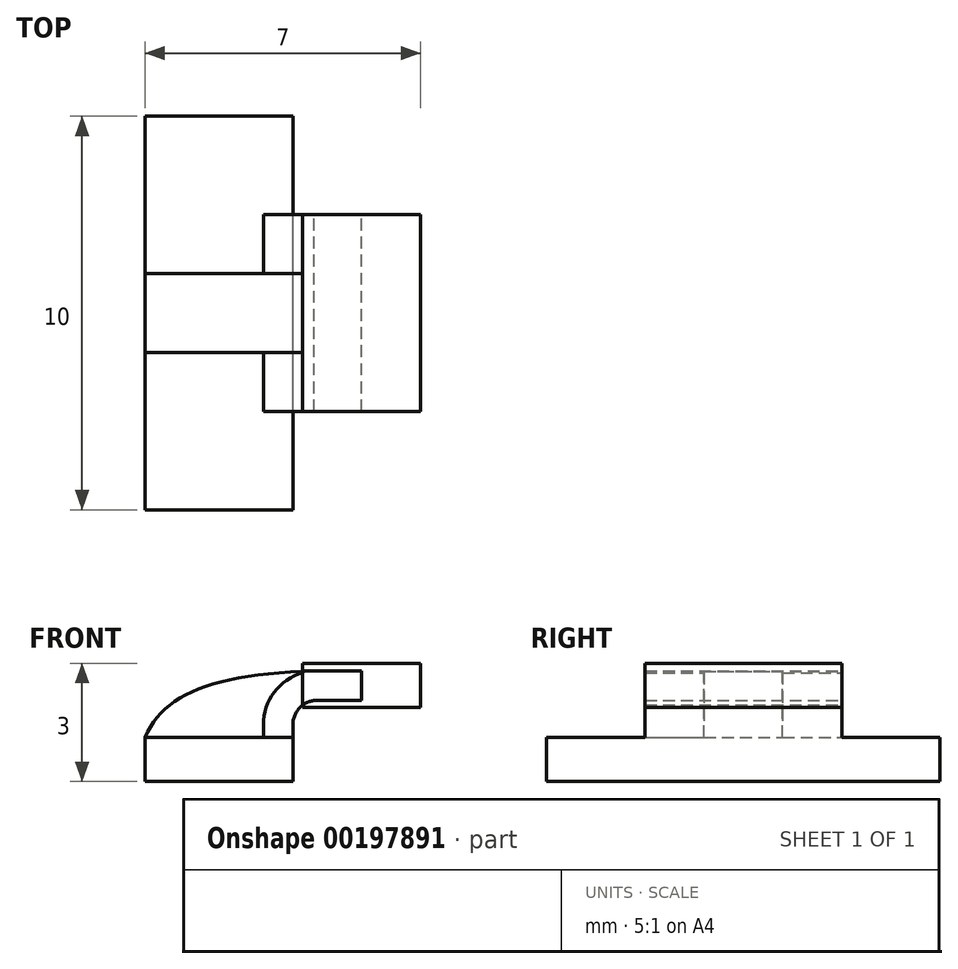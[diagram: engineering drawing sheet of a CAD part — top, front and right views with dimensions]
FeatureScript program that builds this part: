
annotation { "Feature Type Name" : "Feature", "Feature Type Description" : "" }
export const myFeature = defineFeature(function(context is Context, id is Id, definition is map)
    precondition{}
    {
        {
            var Q0;
            Q0=qCreatedBy(makeId("Front.planeOp"),FACE);
            var sketch = newSketch(context, id + "F0", { "sketchPlane" : qUnion([Q0])});
            skLineSegment(sketch, "E0.bottom", {"start": v(-1.87, -0.56) * mm, "end": v(1.88, -0.56) * mm});
            skLineSegment(sketch, "E0.top", {"start": v(-1.88, 0.56) * mm, "end": v(1.87, 0.56) * mm});
            skLineSegment(sketch, "E0.left", {"start": v(-1.87, -0.56) * mm, "end": v(-1.88, 0.56) * mm});
            skLineSegment(sketch, "E0.right", {"start": v(1.88, -0.56) * mm, "end": v(1.87, 0.56) * mm});
            skPoint(sketch, "E0.middle", {"position": v(0, 0) * mm});
            skLineSegment(sketch, "E1.bottom", {"start": v(2.12, 1.31) * mm, "end": v(5.12, 1.31) * mm});
            skLineSegment(sketch, "E1.top", {"start": v(2.12, 2.44) * mm, "end": v(5.12, 2.44) * mm});
            skLineSegment(sketch, "E1.left", {"start": v(2.12, 1.31) * mm, "end": v(2.12, 2.44) * mm});
            skLineSegment(sketch, "E1.right", {"start": v(5.12, 1.31) * mm, "end": v(5.12, 2.44) * mm});
            skPoint(sketch, "E1.middle", {"position": v(3.62, 1.87) * mm});
            skLineSegment(sketch, "E2", {"start": v(1.87, 0.56) * mm, "end": v(1.87, 0.88) * mm});
            skArc(sketch, "E3", {"start": v(1.87, 0.88) * mm, "mid": v(2.06, 1.32) * mm, "end": v(2.5, 1.5) * mm});
            skLineSegment(sketch, "E4", {"start": v(2.5, 1.5) * mm, "end": v(3.62, 1.5) * mm});
            skPoint(sketch, "E4.endSnap0", {"position": v(3.62, 1.31) * mm});
            skLineSegment(sketch, "E5.0", {"start": v(2.5, -3.5) * mm, "end": v(3.62, -3.5) * mm});
            skLineSegment(sketch, "E6.0", {"start": v(2.5, 2.25) * mm, "end": v(3.62, 2.25) * mm});
            skArc(sketch, "E6.1", {"start": v(1.12, 0.88) * mm, "mid": v(1.53, 1.85) * mm, "end": v(2.5, 2.25) * mm});
            skLineSegment(sketch, "E6.2", {"start": v(1.12, 0.56) * mm, "end": v(1.12, 0.88) * mm});
            skLineSegment(sketch, "E7", {"start": v(3.62, 1.5) * mm, "end": v(3.62, 2.25) * mm});
            skFitSpline(sketch, "E8", {"points": [v(-1.88, 0.56) * mm, v(2.5, 2.25) * mm], "startDerivative": vector(1.4, 3.3) * mm, "endDerivative": vector(7.91, 0.22) * mm});
            skSolve(sketch);
        }
        {
            var Q0;
            Q0=makeQuery(id+"F0.imprint","IMPRINT",FACE,{"disambiguationData":[TD([[makeQuery(id+"F0.imprint","IMPRINT",EDGE,{"derivedFrom":sQuery(id+"F0.wireOp",EDGE,"E0.bottom")}),1.0]])]});
            extrude(context, id + "F1", {"entities" : qUnion([Q0]), "endBound" : BoundingType.SYMMETRIC, "depth" : 10 * mm});
        }
        {
            var Q0;
            {var subQ8=sQuery(id+"F0.wireOp",EDGE,"E1.bottom");Q0=makeQuery(id+"F0.imprint","IMPRINT",FACE,{"disambiguationData":[TD([[makeQuery(id+"F0.imprint","IMPRINT",EDGE,{"derivedFrom":subQ8}),1.0]])]});}
            var Q1;
            {var subQ1=sQuery(id+"F0.wireOp",EDGE,"E2");Q1=makeQuery(id+"F0.imprint","IMPRINT",FACE,{"disambiguationData":[TD([[makeQuery(id+"F0.imprint","IMPRINT",EDGE,{"derivedFrom":subQ1}),1.0]])]});}
            extrude(context, id + "F2", {"entities" : qUnion([Q0, Q1]), "operationType" : NewBodyOperationType.ADD, "endBound" : BoundingType.SYMMETRIC, "depth" : 5 * mm});
        }
        {
            var Q0;
            {var subQ0=sQuery(id+"F0.wireOp",EDGE,"E6.2");Q0=makeQuery(id+"F0.imprint","IMPRINT",FACE,{"disambiguationData":[TD([[makeQuery(id+"F0.imprint","IMPRINT",EDGE,{"derivedFrom":subQ0}),1.0]])]});}
            extrude(context, id + "F3", {"entities" : qUnion([Q0]), "operationType" : NewBodyOperationType.ADD, "endBound" : BoundingType.SYMMETRIC, "depth" : 2 * mm});
        }
    });
